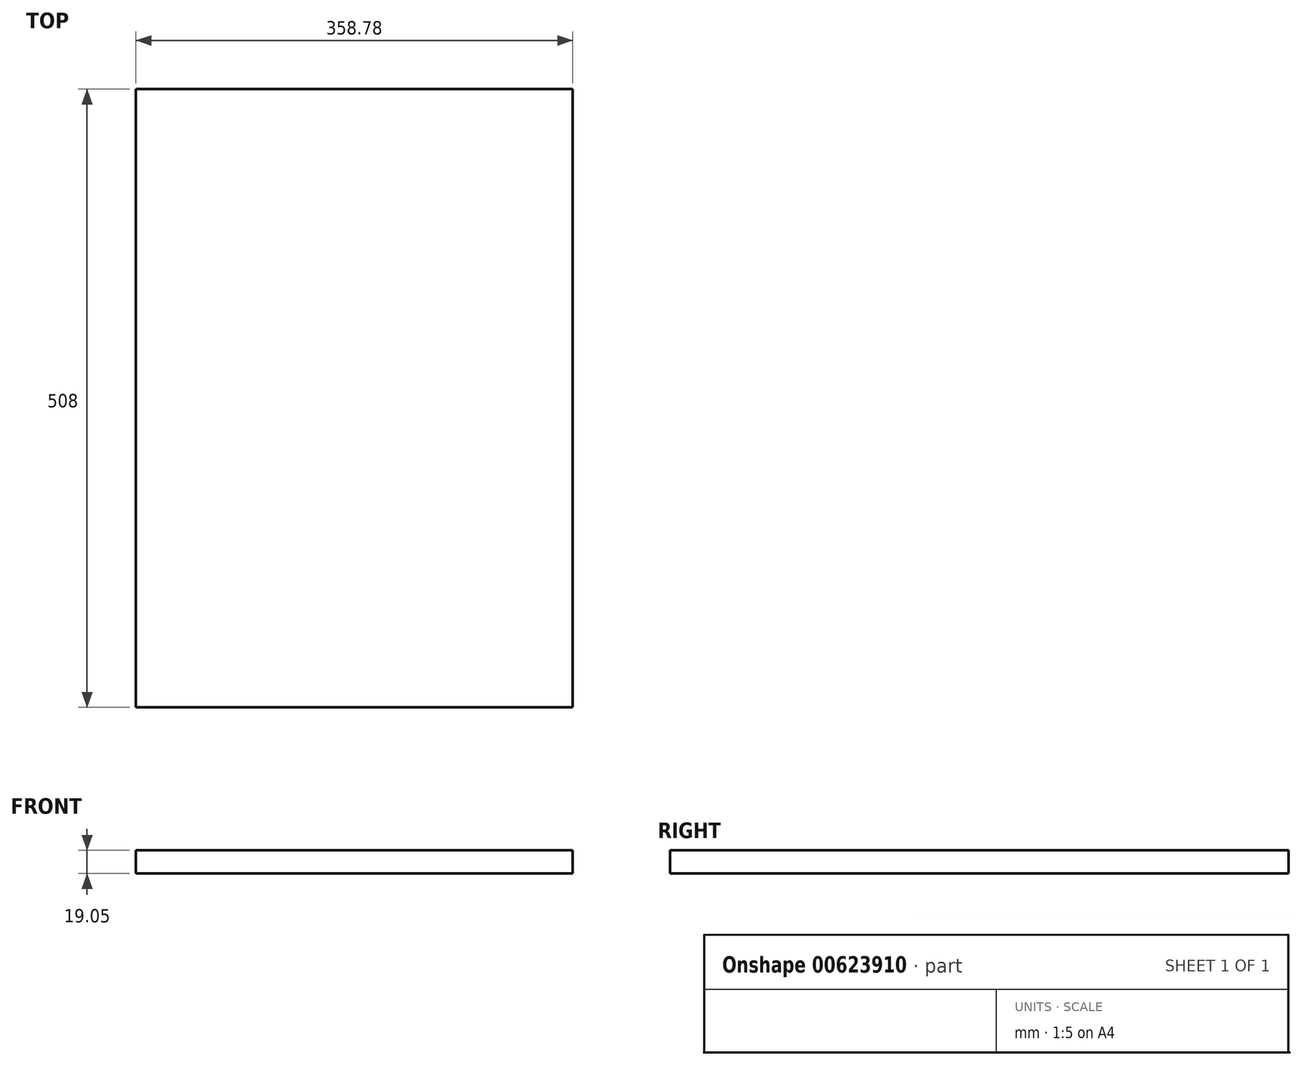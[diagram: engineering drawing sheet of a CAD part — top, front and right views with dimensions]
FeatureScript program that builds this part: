
annotation { "Feature Type Name" : "Feature", "Feature Type Description" : "" }
export const myFeature = defineFeature(function(context is Context, id is Id, definition is map)
    precondition{}
    {
        {
            var Q0;
            Q0=qCreatedBy(makeId("Top.planeOp"),FACE);
            var sketch = newSketch(context, id + "F0", { "sketchPlane" : qUnion([Q0])});
            skLineSegment(sketch, "E0.bottom", {"start": v(179.39, 254) * mm, "end": v(-179.39, 254) * mm});
            skLineSegment(sketch, "E0.top", {"start": v(179.39, -254) * mm, "end": v(-179.39, -254) * mm});
            skLineSegment(sketch, "E0.left", {"start": v(179.39, 254) * mm, "end": v(179.39, -254) * mm});
            skLineSegment(sketch, "E0.right", {"start": v(-179.39, 254) * mm, "end": v(-179.39, -254) * mm});
            skPoint(sketch, "E0.middle", {"position": v(0, 0) * mm});
            skSolve(sketch);
        }
        {
            var Q0;
            Q0=makeQuery(id+"F0.imprint","IMPRINT",FACE,{"disambiguationData":[TD([[makeQuery(id+"F0.imprint","IMPRINT",EDGE,{"derivedFrom":sQuery(id+"F0.wireOp",EDGE,"E0.bottom")}),1.0]])]});
            extrude(context, id + "F1", {"entities" : qUnion([Q0]), "depth" : 19.05 * mm, "offsetDistance" : 25.4 * mm});
        }
    });
